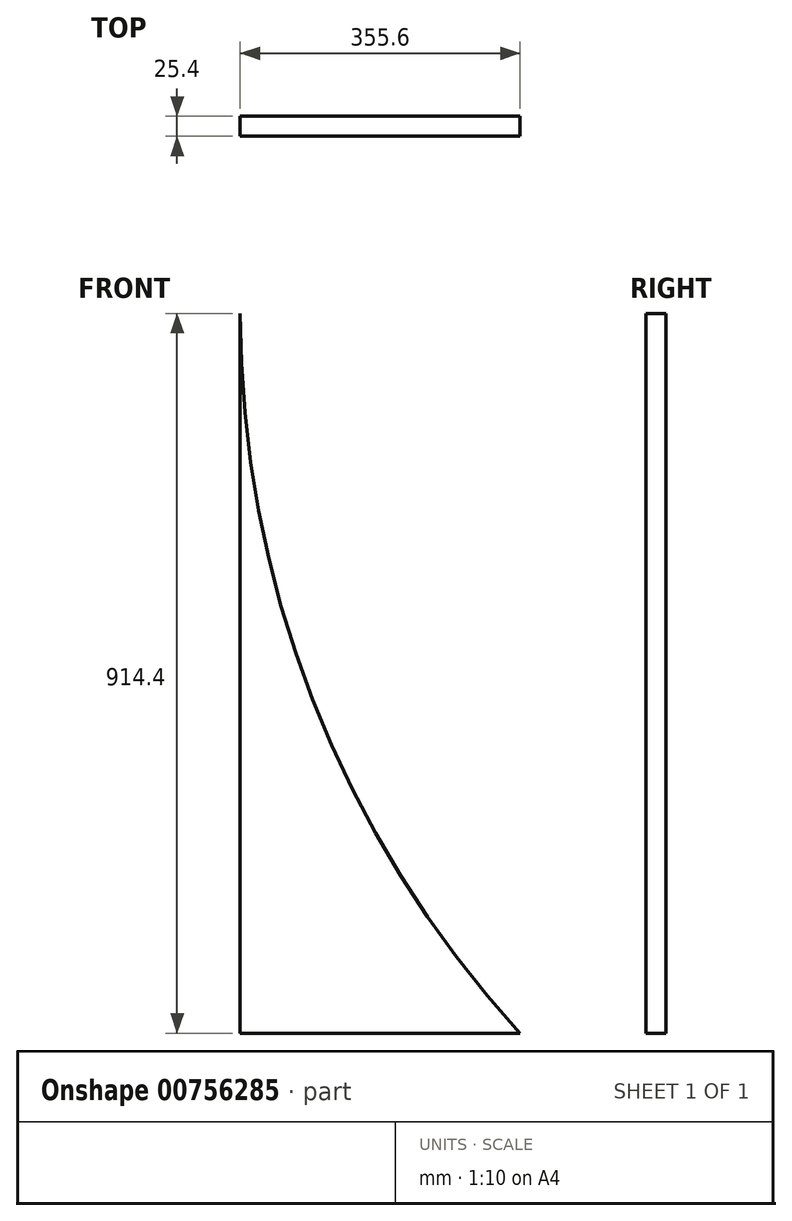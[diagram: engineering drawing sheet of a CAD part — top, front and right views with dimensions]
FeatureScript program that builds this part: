
annotation { "Feature Type Name" : "Feature", "Feature Type Description" : "" }
export const myFeature = defineFeature(function(context is Context, id is Id, definition is map)
    precondition{}
    {
        {
            var Q0;
            Q0=qCreatedBy(makeId("Front.planeOp"),FACE);
            var sketch = newSketch(context, id + "F0", { "sketchPlane" : qUnion([Q0])});
            skLineSegment(sketch, "E0", {"start": v(0, 0) * mm, "end": v(0, 914.4) * mm});
            skLineSegment(sketch, "E1", {"start": v(0, 0) * mm, "end": v(355.6, 0) * mm});
            skArc(sketch, "E2", {"start": v(0, 914.4) * mm, "mid": v(92.03, 423.84) * mm, "end": v(355.6, 0) * mm});
            skSolve(sketch);
        }
        {
            var Q0;
            Q0 = qSketchRegion(id + "F0", true);
            extrude(context, id + "F1", {"entities" : qUnion([Q0]), "depth" : 25.4 * mm, "offsetDistance" : 25.4 * mm});
        }
    });
